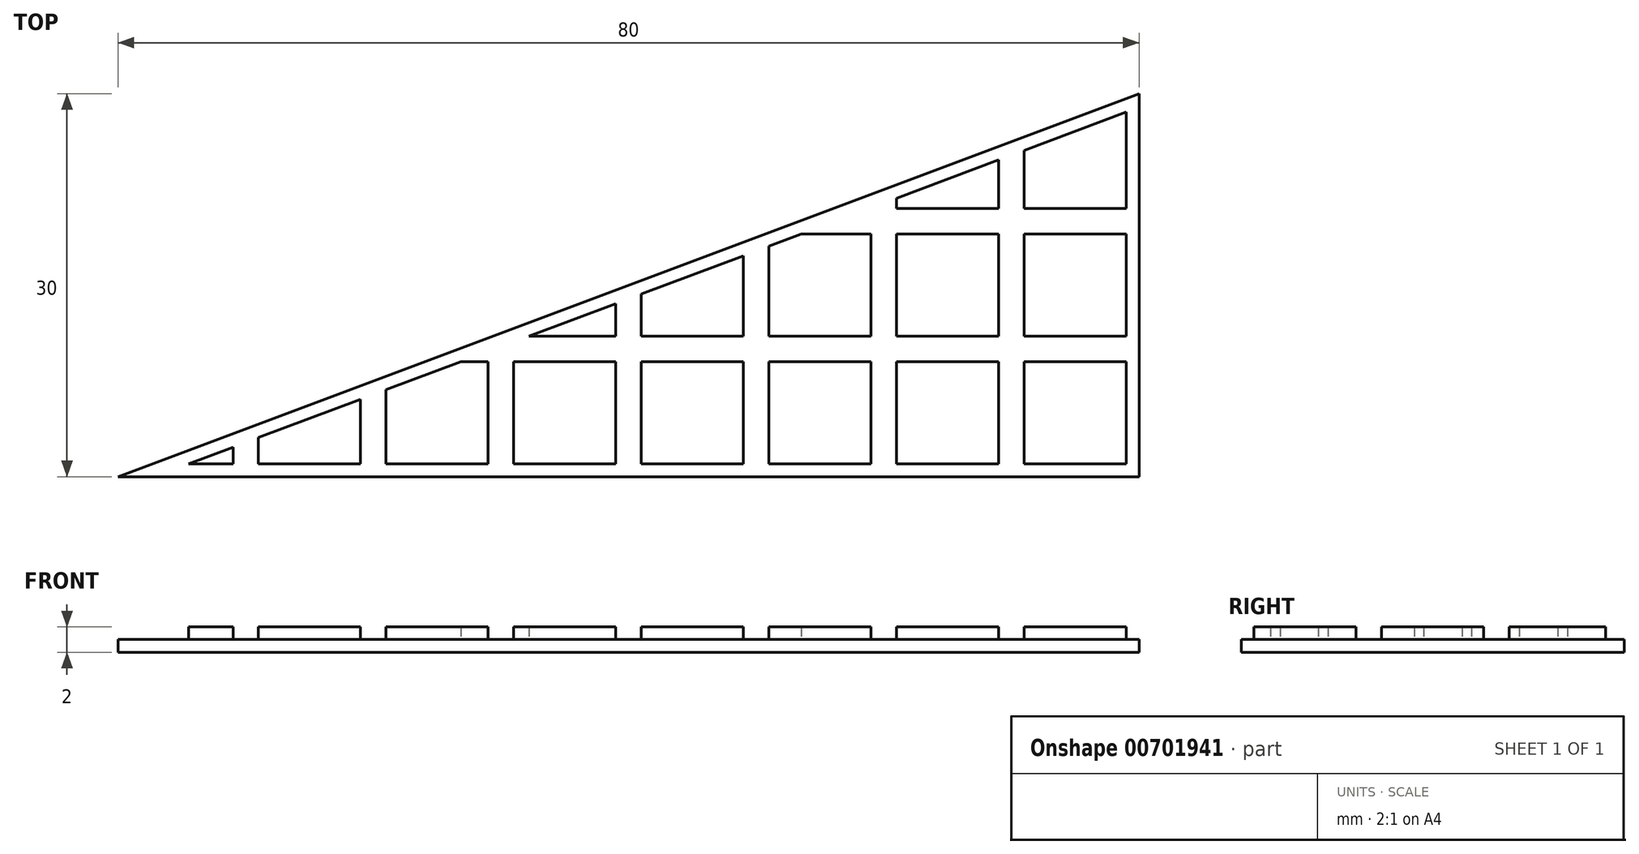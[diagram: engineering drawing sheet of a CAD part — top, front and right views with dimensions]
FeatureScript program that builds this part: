
annotation { "Feature Type Name" : "Feature", "Feature Type Description" : "" }
export const myFeature = defineFeature(function(context is Context, id is Id, definition is map)
    precondition{}
    {
        {
            var Q0;
            Q0=qCreatedBy(makeId("Top.planeOp"),FACE);
            var sketch = newSketch(context, id + "F0", { "sketchPlane" : qUnion([Q0])});
            skLineSegment(sketch, "E0", {"start": v(-43.47, 14.9) * mm, "end": v(36.53, 14.9) * mm});
            skLineSegment(sketch, "E1", {"start": v(36.53, 14.9) * mm, "end": v(36.53, 44.9) * mm});
            skLineSegment(sketch, "E2", {"start": v(36.53, 44.9) * mm, "end": v(-43.47, 14.9) * mm});
            skSolve(sketch);
        }
        {
            var Q0;
            Q0 = qSketchRegion(id + "F0", true);
            extrude(context, id + "F1", {"entities" : qUnion([Q0]), "depth" : 1 * mm, "offsetDistance" : 25 * mm});
        }
        {
            var Q0;
            Q0=makeQuery(id+"F1.opExtrude","CAP_FACE",FACE,{"disambiguationData":[OSD([sQuery(id+"F0.wireOp",EDGE,"E0"),sQuery(id+"F0.wireOp",EDGE,"E1"),sQuery(id+"F0.wireOp",EDGE,"E2")])],"isStart":false});
            var sketch = newSketch(context, id + "F2", { "sketchPlane" : qUnion([Q0])});
            skLineSegment(sketch, "E3", {"start": v(35.53, 43.45) * mm, "end": v(35.53, 15.9) * mm});
            skLineSegment(sketch, "E4", {"start": v(35.53, 15.9) * mm, "end": v(-37.95, 15.9) * mm});
            skLineSegment(sketch, "E5", {"start": v(-37.95, 15.9) * mm, "end": v(35.53, 43.45) * mm});
            skLineSegment(sketch, "E6", {"start": v(26.53, 41.14) * mm, "end": v(26.53, 15.9) * mm, "construction": true});
            skLineSegment(sketch, "E7", {"start": v(16.53, 36.32) * mm, "end": v(16.53, 15.9) * mm, "construction": true});
            skLineSegment(sketch, "E8", {"start": v(6.53, 32.57) * mm, "end": v(6.53, 15.9) * mm, "construction": true});
            skLineSegment(sketch, "E9", {"start": v(-3.47, 28.82) * mm, "end": v(-3.47, 15.9) * mm, "construction": true});
            skLineSegment(sketch, "E10", {"start": v(-13.47, 25.07) * mm, "end": v(-13.47, 15.9) * mm, "construction": true});
            skLineSegment(sketch, "E11", {"start": v(-23.47, 21.32) * mm, "end": v(-23.47, 15.9) * mm, "construction": true});
            skLineSegment(sketch, "E12", {"start": v(-33.47, 17.57) * mm, "end": v(-33.47, 15.9) * mm, "construction": true});
            skLineSegment(sketch, "E13", {"start": v(35.53, 34.9) * mm, "end": v(12.72, 34.9) * mm, "construction": true});
            skLineSegment(sketch, "E14", {"start": v(35.53, 24.9) * mm, "end": v(-13.95, 24.9) * mm, "construction": true});
            skLineSegment(sketch, "E15", {"start": v(27.53, 40.45) * mm, "end": v(27.53, 15.9) * mm});
            skLineSegment(sketch, "E16", {"start": v(25.53, 15.9) * mm, "end": v(25.53, 39.7) * mm});
            skLineSegment(sketch, "E17", {"start": v(35.53, 35.9) * mm, "end": v(15.38, 35.9) * mm});
            skLineSegment(sketch, "E18", {"start": v(10.05, 33.9) * mm, "end": v(35.53, 33.9) * mm});
            skLineSegment(sketch, "E19", {"start": v(17.53, 15.9) * mm, "end": v(17.53, 36.7) * mm});
            skLineSegment(sketch, "E20", {"start": v(15.53, 15.9) * mm, "end": v(15.53, 35.95) * mm});
            skLineSegment(sketch, "E21", {"start": v(35.53, 25.9) * mm, "end": v(-11.28, 25.9) * mm});
            skLineSegment(sketch, "E22", {"start": v(35.53, 23.9) * mm, "end": v(-16.62, 23.9) * mm});
            skLineSegment(sketch, "E23", {"start": v(7.53, 32.95) * mm, "end": v(7.53, 15.9) * mm});
            skLineSegment(sketch, "E24", {"start": v(5.53, 15.9) * mm, "end": v(5.53, 32.2) * mm});
            skLineSegment(sketch, "E25", {"start": v(-4.47, 28.45) * mm, "end": v(-4.47, 15.9) * mm});
            skLineSegment(sketch, "E26", {"start": v(-2.47, 29.2) * mm, "end": v(-2.47, 15.9) * mm});
            skLineSegment(sketch, "E27", {"start": v(-12.47, 15.9) * mm, "end": v(-12.47, 25.45) * mm});
            skLineSegment(sketch, "E28", {"start": v(-14.47, 15.9) * mm, "end": v(-14.47, 24.7) * mm});
            skLineSegment(sketch, "E29", {"start": v(-22.47, 21.7) * mm, "end": v(-22.47, 15.9) * mm});
            skLineSegment(sketch, "E30", {"start": v(-24.47, 20.95) * mm, "end": v(-24.47, 15.9) * mm});
            skLineSegment(sketch, "E31", {"start": v(-32.47, 17.95) * mm, "end": v(-32.47, 15.9) * mm});
            skLineSegment(sketch, "E32", {"start": v(-34.47, 17.2) * mm, "end": v(-34.47, 15.9) * mm});
            skSolve(sketch);
        }
        {
            var Q0;
            {var subQ3=sQuery(id+"F2.wireOp",EDGE,"E32");Q0=makeQuery(id+"F2.imprint","IMPRINT",FACE,{"disambiguationData":[TD([[makeQuery(id+"F2.imprint","IMPRINT",EDGE,{"derivedFrom":subQ3}),-1.0]])]});}
            var Q1;
            {var subQ0=sQuery(id+"F2.wireOp",EDGE,"E30");Q1=makeQuery(id+"F2.imprint","IMPRINT",FACE,{"disambiguationData":[TD([[makeQuery(id+"F2.imprint","IMPRINT",EDGE,{"derivedFrom":subQ0}),-1.0]])]});}
            var Q2;
            {var subQ5=sQuery(id+"F2.wireOp",EDGE,"E29");Q2=makeQuery(id+"F2.imprint","IMPRINT",FACE,{"disambiguationData":[TD([[makeQuery(id+"F2.imprint","IMPRINT",EDGE,{"derivedFrom":subQ5}),1.0]])]});}
            var Q3;
            {var subQ0=sQuery(id+"F2.wireOp",EDGE,"E25");var subQ1=sQuery(id+"F2.wireOp",EDGE,"E4");var subQ2=makeQuery(id+"F2.imprint","INTERSECT",VERTEX,{"derivedFrom":[subQ1,subQ0]});Q3=makeQuery(id+"F2.imprint","IMPRINT",FACE,{"disambiguationData":[TD([[makeQuery(id+"F2.imprint","IMPRINT",EDGE,{"disambiguationData":[TD([[subQ2,-1.0]])],"derivedFrom":subQ1}),-1.0]])]});}
            var Q4;
            {var subQ0=sQuery(id+"F2.wireOp",EDGE,"E21");var subQ1=sQuery(id+"F2.wireOp",EDGE,"E5");var subQ2=makeQuery(id+"F2.imprint","INTERSECT",VERTEX,{"derivedFrom":[subQ1,subQ0]});Q4=makeQuery(id+"F2.imprint","IMPRINT",FACE,{"disambiguationData":[TD([[makeQuery(id+"F2.imprint","IMPRINT",EDGE,{"disambiguationData":[TD([[subQ2,-1.0]])],"derivedFrom":subQ1}),-1.0]])]});}
            var Q5;
            {var subQ0=sQuery(id+"F2.wireOp",EDGE,"E24");var subQ1=sQuery(id+"F2.wireOp",EDGE,"E5");var subQ2=makeQuery(id+"F2.imprint","INTERSECT",VERTEX,{"derivedFrom":[subQ1,subQ0]});Q5=makeQuery(id+"F2.imprint","IMPRINT",FACE,{"disambiguationData":[TD([[makeQuery(id+"F2.imprint","IMPRINT",EDGE,{"disambiguationData":[TD([[subQ2,1.0]])],"derivedFrom":subQ1}),-1.0]])]});}
            var Q6;
            {var subQ0=sQuery(id+"F2.wireOp",EDGE,"E24");var subQ1=sQuery(id+"F2.wireOp",EDGE,"E4");var subQ2=makeQuery(id+"F2.imprint","INTERSECT",VERTEX,{"derivedFrom":[subQ1,subQ0]});Q6=makeQuery(id+"F2.imprint","IMPRINT",FACE,{"disambiguationData":[TD([[makeQuery(id+"F2.imprint","IMPRINT",EDGE,{"disambiguationData":[TD([[subQ2,-1.0]])],"derivedFrom":subQ1}),-1.0]])]});}
            var Q7;
            {var subQ5=sQuery(id+"F2.wireOp",EDGE,"E18");var subQ7=sQuery(id+"F2.wireOp",EDGE,"E5");var subQ8=makeQuery(id+"F2.imprint","INTERSECT",VERTEX,{"derivedFrom":[subQ7,subQ5]});Q7=makeQuery(id+"F2.imprint","IMPRINT",FACE,{"disambiguationData":[TD([[makeQuery(id+"F2.imprint","IMPRINT",EDGE,{"disambiguationData":[TD([[subQ8,1.0]])],"derivedFrom":subQ7}),-1.0]])]});}
            var Q8;
            {var subQ0=sQuery(id+"F2.wireOp",EDGE,"E20");var subQ1=sQuery(id+"F2.wireOp",EDGE,"E4");var subQ2=makeQuery(id+"F2.imprint","INTERSECT",VERTEX,{"derivedFrom":[subQ1,subQ0]});Q8=makeQuery(id+"F2.imprint","IMPRINT",FACE,{"disambiguationData":[TD([[makeQuery(id+"F2.imprint","IMPRINT",EDGE,{"disambiguationData":[TD([[subQ2,-1.0]])],"derivedFrom":subQ1}),-1.0]])]});}
            var Q9;
            {var subQ0=sQuery(id+"F2.wireOp",EDGE,"E21");var subQ1=sQuery(id+"F2.wireOp",EDGE,"E16");var subQ2=makeQuery(id+"F2.imprint","INTERSECT",VERTEX,{"derivedFrom":[subQ1,subQ0]});Q9=makeQuery(id+"F2.imprint","IMPRINT",FACE,{"disambiguationData":[TD([[makeQuery(id+"F2.imprint","IMPRINT",EDGE,{"disambiguationData":[TD([[subQ2,-1.0]])],"derivedFrom":subQ1}),1.0]])]});}
            var Q10;
            {var subQ0=sQuery(id+"F2.wireOp",EDGE,"E16");var subQ1=sQuery(id+"F2.wireOp",EDGE,"E5");var subQ2=makeQuery(id+"F2.imprint","INTERSECT",VERTEX,{"derivedFrom":[subQ1,subQ0]});Q10=makeQuery(id+"F2.imprint","IMPRINT",FACE,{"disambiguationData":[TD([[makeQuery(id+"F2.imprint","IMPRINT",EDGE,{"disambiguationData":[TD([[subQ2,1.0]])],"derivedFrom":subQ1}),-1.0]])]});}
            var Q11;
            {var subQ0=sQuery(id+"F2.wireOp",EDGE,"E16");var subQ1=sQuery(id+"F2.wireOp",EDGE,"E4");var subQ2=makeQuery(id+"F2.imprint","INTERSECT",VERTEX,{"derivedFrom":[subQ1,subQ0]});Q11=makeQuery(id+"F2.imprint","IMPRINT",FACE,{"disambiguationData":[TD([[makeQuery(id+"F2.imprint","IMPRINT",EDGE,{"disambiguationData":[TD([[subQ2,-1.0]])],"derivedFrom":subQ1}),-1.0]])]});}
            var Q12;
            {var subQ0=sQuery(id+"F2.wireOp",EDGE,"E5");var subQ1=sQuery(id+"F2.wireOp",EDGE,"E3");var subQ2=makeQuery(id+"F2.imprint","INTERSECT",VERTEX,{"derivedFrom":[subQ1,subQ0]});Q12=makeQuery(id+"F2.imprint","IMPRINT",FACE,{"disambiguationData":[TD([[makeQuery(id+"F2.imprint","IMPRINT",EDGE,{"disambiguationData":[TD([[subQ2,-1.0]])],"derivedFrom":subQ1}),-1.0]])]});}
            var Q13;
            {var subQ0=sQuery(id+"F2.wireOp",EDGE,"E18");var subQ1=sQuery(id+"F2.wireOp",EDGE,"E3");var subQ2=makeQuery(id+"F2.imprint","INTERSECT",VERTEX,{"derivedFrom":[subQ1,subQ0]});Q13=makeQuery(id+"F2.imprint","IMPRINT",FACE,{"disambiguationData":[TD([[makeQuery(id+"F2.imprint","IMPRINT",EDGE,{"disambiguationData":[TD([[subQ2,-1.0]])],"derivedFrom":subQ1}),-1.0]])]});}
            var Q14;
            {var subQ0=sQuery(id+"F2.wireOp",EDGE,"E4");var subQ1=sQuery(id+"F2.wireOp",EDGE,"E3");var subQ2=makeQuery(id+"F2.imprint","INTERSECT",VERTEX,{"derivedFrom":[subQ1,subQ0]});Q14=makeQuery(id+"F2.imprint","IMPRINT",FACE,{"disambiguationData":[TD([[makeQuery(id+"F2.imprint","IMPRINT",EDGE,{"disambiguationData":[TD([[subQ2,1.0]])],"derivedFrom":subQ1}),-1.0]])]});}
            extrude(context, id + "F3", {"entities" : qUnion([Q0, Q1, Q2, Q3, Q4, Q5, Q6, Q7, Q8, Q9, Q10, Q11, Q12, Q13, Q14]), "operationType" : NewBodyOperationType.ADD, "depth" : 1 * mm, "offsetDistance" : 25 * mm});
        }
    });
